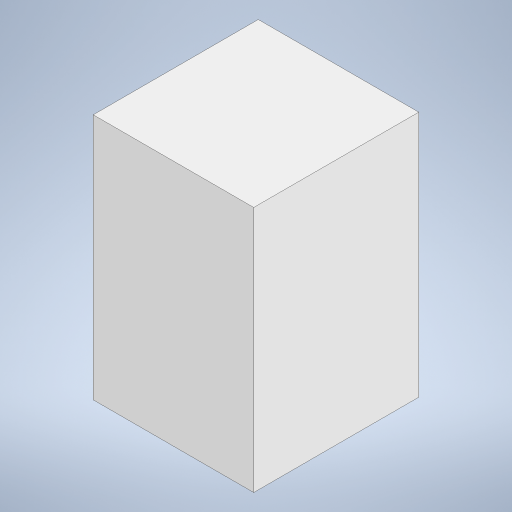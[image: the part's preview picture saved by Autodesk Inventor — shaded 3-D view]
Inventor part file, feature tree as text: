
AUTODESK INVENTOR PART (.ipt)
format: ipt  version: 2024 (Build 280153000, 153)  size: 174,592 bytes
history: native  units: in
note: dims shown in document units (in); Inventor stores cm internally (conversion verified against a paired STEP export)
features: extrude x1, sketch x1
ambient origin geometry x8: Origin, YZ Plane, XZ Plane, XY Plane, X Axis, Y Axis, Z Axis, Center Point
bodies: Solid1 (feature_tree)
feature tree (2):
  extrude  "Extrusion1"  Depth=29.0in
  sketch  "Sketch1"  dims[d1=43.375in d2=29.0in d3=28.2in d4=0.0in]
